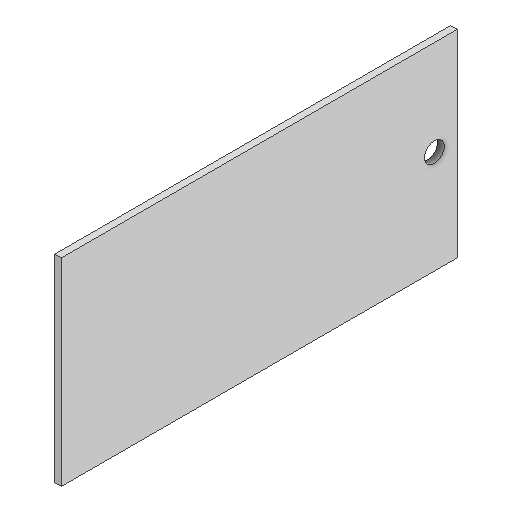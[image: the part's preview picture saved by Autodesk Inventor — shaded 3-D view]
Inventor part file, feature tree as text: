
AUTODESK INVENTOR PART (.ipt)
format: ipt  version: 2022 (Build 260153000, 153)  size: 89,600 bytes
history: native  units: mm
features: extrude x2, sketch x2
ambient origin geometry x8: Origin, YZ Plane, XZ Plane, XY Plane, X Axis, Y Axis, Z Axis, Center Point
bodies: Solid1 (feature_tree)
feature tree (4):
  extrude  "Extrusion1"  Depth=300.0mm
  extrude  "Extrusion2"  Depth=5.0mm
  sketch  "Sketch1"  dims[d0=150.0mm d1=300.0mm]
  sketch  "Sketch2"  dims[d2=5.0mm d3=0.0mm d4=15.0mm d5=0.0mm d6=0.0mm d7=0.5mm d8=0.872665mm]
